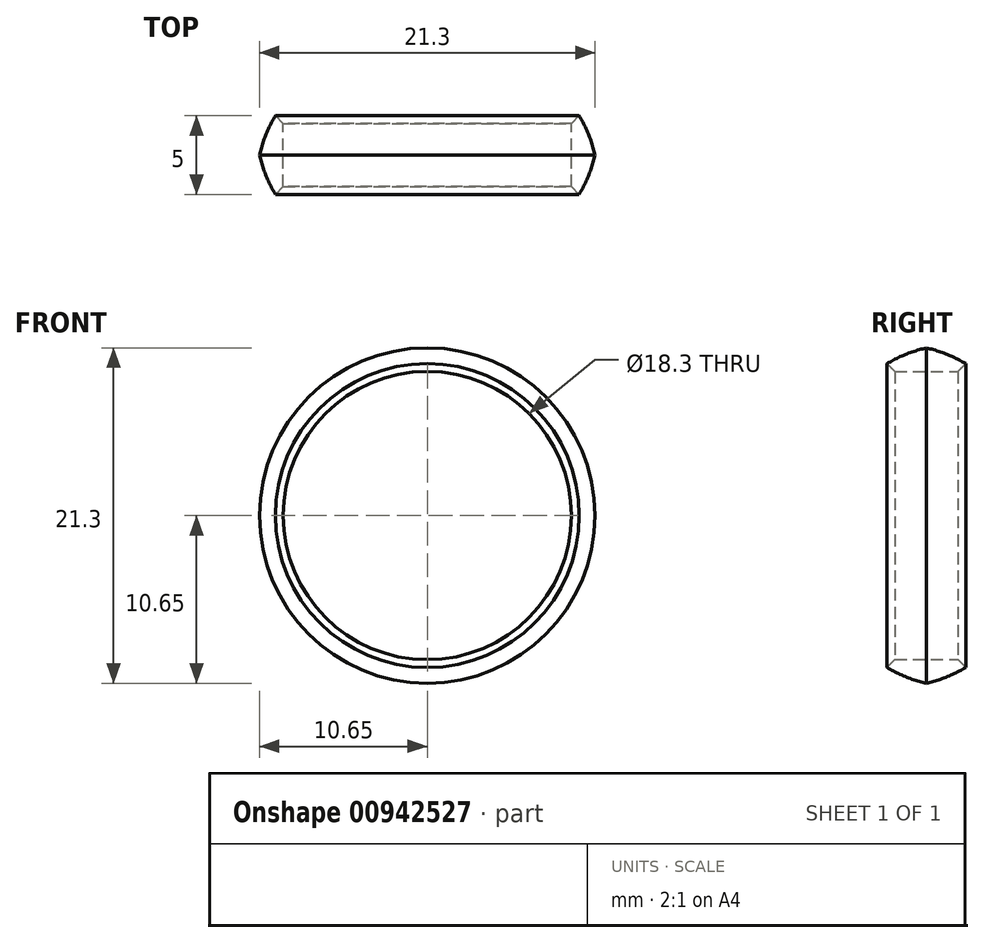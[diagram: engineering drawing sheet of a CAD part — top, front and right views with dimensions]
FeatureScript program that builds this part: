
annotation { "Feature Type Name" : "Feature", "Feature Type Description" : "" }
export const myFeature = defineFeature(function(context is Context, id is Id, definition is map)
    precondition{}
    {
        {
            var Q0;
            Q0=qCreatedBy(makeId("Front.planeOp"),FACE);
            var sketch = newSketch(context, id + "F0", { "sketchPlane" : qUnion([Q0])});
            skCircle(sketch, "E0", {"center": v(0, 0) * mm, "radius": 9.23 * mm});
            skSolve(sketch);
        }
        {
            var Q0;
            Q0=qCreatedBy(makeId("Right.planeOp"),FACE);
            var sketch = newSketch(context, id + "F1", { "sketchPlane" : qUnion([Q0])});
            skLineSegment(sketch, "E1", {"start": v(0, 9.15) * mm, "end": v(2.5, 9.15) * mm});
            skLineSegment(sketch, "E2", {"start": v(2.5, 9.15) * mm, "end": v(2.5, 9.65) * mm});
            skLineSegment(sketch, "E3", {"start": v(0, 9.15) * mm, "end": v(0, 10.65) * mm, "construction": true});
            skArc(sketch, "E4", {"start": v(2.5, 9.65) * mm, "mid": v(1.29, 10.25) * mm, "end": v(0, 10.65) * mm});
            skLineSegment(sketch, "E5.MirrorCS", {"start": v(-2.5, 9.15) * mm, "end": v(-2.5, 9.65) * mm});
            skLineSegment(sketch, "E6.MirrorCS", {"start": v(0, 9.15) * mm, "end": v(-2.5, 9.15) * mm});
            skArc(sketch, "E7.MirrorCS", {"start": v(-2.5, 9.65) * mm, "mid": v(-1.29, 10.25) * mm, "end": v(0, 10.65) * mm});
            skSolve(sketch);
        }
        {
            var Q0;
            Q0=makeQuery(id+"F1.imprint","IMPRINT",FACE,{"disambiguationData":[TD([[makeQuery(id+"F1.imprint","IMPRINT",EDGE,{"derivedFrom":sQuery(id+"F1.wireOp",EDGE,"E1")}),1.0]])]});
            var Q1;
            Q1=sQuery(id+"F0.wireOp",EDGE,"E0");
            revolve(context, id + "F2", {"surfaceOperationType" : NewSurfaceOperationType.NEW, "entities" : qUnion([Q0]), "axis" : qUnion([Q1]), "revolveType" : RevolveType.FULL});
        }
        {
            var Q0;
            Q0=makeQuery(id+"F2.opRevolve","SWEPT_EDGE",EDGE,{"disambiguationData":[OSD([sQuery(id+"F1.wireOp",EDGE,"E5.MirrorCS"),sQuery(id+"F1.wireOp",EDGE,"E6.MirrorCS")])]});
            var Q1;
            Q1=makeQuery(id+"F2.opRevolve","SWEPT_EDGE",EDGE,{"disambiguationData":[OSD([sQuery(id+"F1.wireOp",EDGE,"E1"),sQuery(id+"F1.wireOp",EDGE,"E2")])]});
            chamfer(context, id + "F3", {"entities" : qUnion([Q0, Q1]), "width" : .5 * mm, "tangentPropagation" : true});
        }
    });
